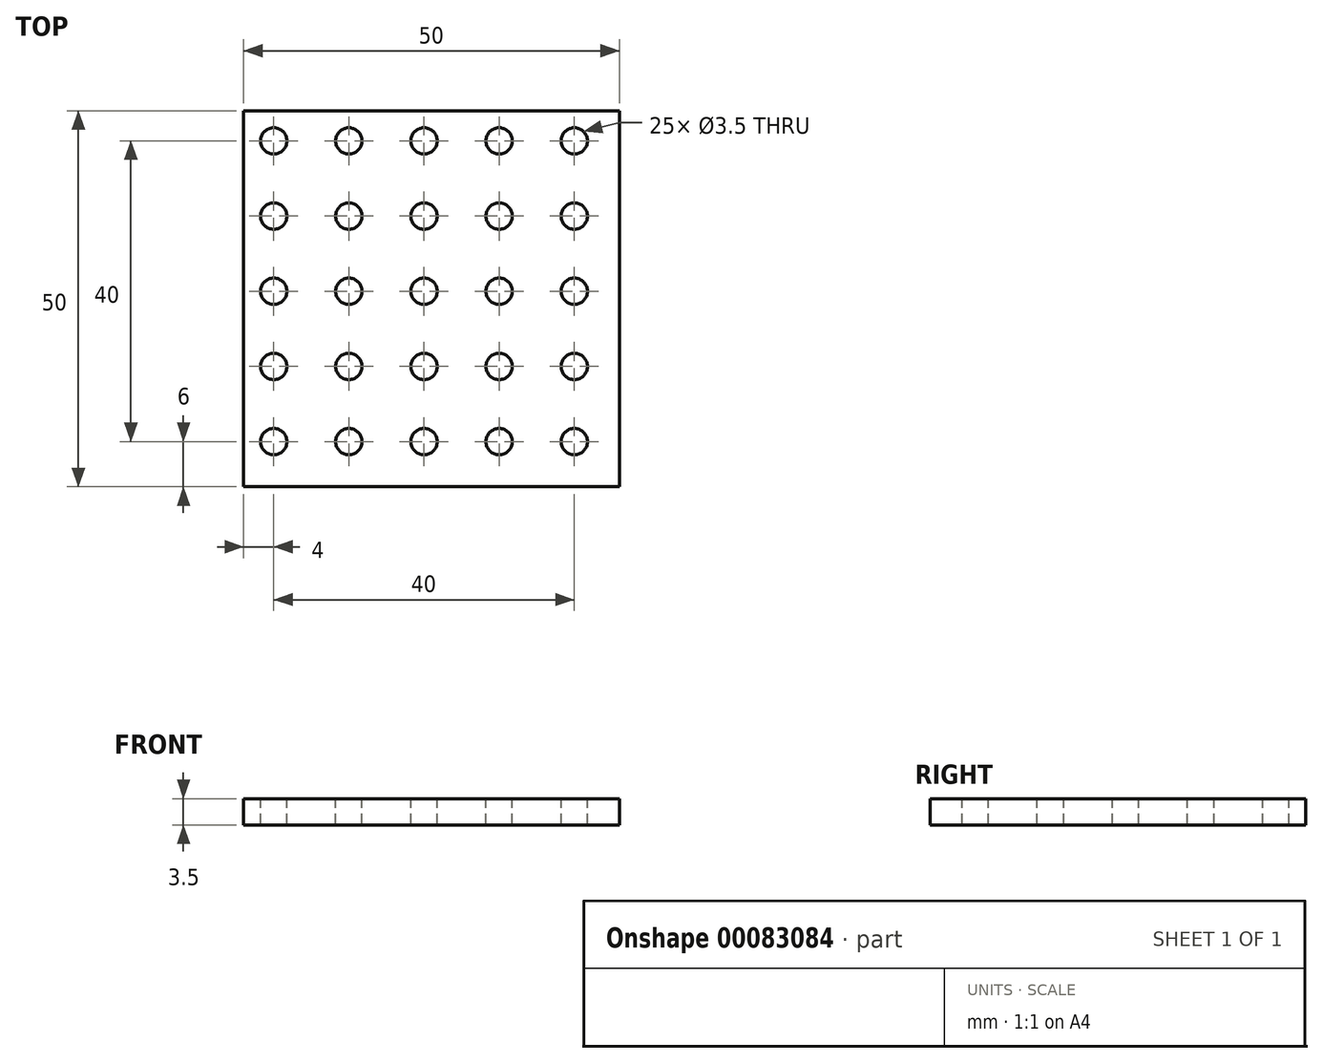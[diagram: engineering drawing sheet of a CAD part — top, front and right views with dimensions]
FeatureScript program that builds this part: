
annotation { "Feature Type Name" : "Feature", "Feature Type Description" : "" }
export const myFeature = defineFeature(function(context is Context, id is Id, definition is map)
    precondition{}
    {
        {
            var Q0;
            Q0=qCreatedBy(makeId("Top.planeOp"),FACE);
            var sketch = newSketch(context, id + "F0", { "sketchPlane" : qUnion([Q0])});
            skLineSegment(sketch, "E0", {"start": v(0, 0) * mm, "end": v(50, 0) * mm});
            skLineSegment(sketch, "E1", {"start": v(50, 0) * mm, "end": v(50, -50) * mm});
            skLineSegment(sketch, "E2", {"start": v(50, -50) * mm, "end": v(0, -50) * mm});
            skLineSegment(sketch, "E3", {"start": v(0, -50) * mm, "end": v(0, 0) * mm});
            skSolve(sketch);
        }
        {
            var Q0;
            Q0=makeQuery(id+"F0.imprint","IMPRINT",FACE,{"disambiguationData":[TD([[makeQuery(id+"F0.imprint","IMPRINT",EDGE,{"derivedFrom":sQuery(id+"F0.wireOp",EDGE,"E0")}),-1.0]])]});
            extrude(context, id + "F1", {"entities" : qUnion([Q0]), "depth" : 3.5 * mm});
        }
        {
            var Q0;
            Q0=makeQuery(id+"F1.opExtrude","CAP_FACE",FACE,{"disambiguationData":[OSD([sQuery(id+"F0.wireOp",EDGE,"E0"),sQuery(id+"F0.wireOp",EDGE,"E1"),sQuery(id+"F0.wireOp",EDGE,"E2"),sQuery(id+"F0.wireOp",EDGE,"E3")])],"isStart":false});
            var sketch = newSketch(context, id + "F2", { "sketchPlane" : qUnion([Q0])});
            skLineSegment(sketch, "E4", {"start": v(0, 0) * mm, "end": v(4, 0) * mm, "construction": true});
            skLineSegment(sketch, "E5", {"start": v(4, 0) * mm, "end": v(4, -4) * mm, "construction": true});
            skCircle(sketch, "E6", {"center": v(4, -4) * mm, "radius": 1.75 * mm});
            skCircle(sketch, "E7.0.1.0", {"center": v(4, -14) * mm, "radius": 1.75 * mm});
            skCircle(sketch, "E7.0.2.0", {"center": v(4, -24) * mm, "radius": 1.75 * mm});
            skCircle(sketch, "E7.0.3.0", {"center": v(4, -34) * mm, "radius": 1.75 * mm});
            skCircle(sketch, "E7.0.4.0", {"center": v(4, -44) * mm, "radius": 1.75 * mm});
            skCircle(sketch, "E7.1.0.0", {"center": v(14, -4) * mm, "radius": 1.75 * mm});
            skCircle(sketch, "E7.1.1.0", {"center": v(14, -14) * mm, "radius": 1.75 * mm});
            skCircle(sketch, "E7.1.2.0", {"center": v(14, -24) * mm, "radius": 1.75 * mm});
            skCircle(sketch, "E7.1.3.0", {"center": v(14, -34) * mm, "radius": 1.75 * mm});
            skCircle(sketch, "E7.1.4.0", {"center": v(14, -44) * mm, "radius": 1.75 * mm});
            skCircle(sketch, "E7.2.0.0", {"center": v(24, -4) * mm, "radius": 1.75 * mm});
            skCircle(sketch, "E7.2.1.0", {"center": v(24, -14) * mm, "radius": 1.75 * mm});
            skCircle(sketch, "E7.2.2.0", {"center": v(24, -24) * mm, "radius": 1.75 * mm});
            skCircle(sketch, "E7.2.3.0", {"center": v(24, -34) * mm, "radius": 1.75 * mm});
            skCircle(sketch, "E7.2.4.0", {"center": v(24, -44) * mm, "radius": 1.75 * mm});
            skCircle(sketch, "E7.3.0.0", {"center": v(34, -4) * mm, "radius": 1.75 * mm});
            skCircle(sketch, "E7.3.1.0", {"center": v(34, -14) * mm, "radius": 1.75 * mm});
            skCircle(sketch, "E7.3.2.0", {"center": v(34, -24) * mm, "radius": 1.75 * mm});
            skCircle(sketch, "E7.3.3.0", {"center": v(34, -34) * mm, "radius": 1.75 * mm});
            skCircle(sketch, "E7.3.4.0", {"center": v(34, -44) * mm, "radius": 1.75 * mm});
            skCircle(sketch, "E7.4.0.0", {"center": v(44, -4) * mm, "radius": 1.75 * mm});
            skCircle(sketch, "E7.4.1.0", {"center": v(44, -14) * mm, "radius": 1.75 * mm});
            skCircle(sketch, "E7.4.2.0", {"center": v(44, -24) * mm, "radius": 1.75 * mm});
            skCircle(sketch, "E7.4.3.0", {"center": v(44, -34) * mm, "radius": 1.75 * mm});
            skCircle(sketch, "E7.4.4.0", {"center": v(44, -44) * mm, "radius": 1.75 * mm});
            skLineSegment(sketch, "E7.direction1", {"start": v(4, -4) * mm, "end": v(14, -4) * mm, "construction": true});
            skLineSegment(sketch, "E7.direction2", {"start": v(4, -4) * mm, "end": v(4, -14) * mm, "construction": true});
            skSolve(sketch);
        }
        {
            var Q0;
            Q0=makeQuery(id+"F2.imprint","IMPRINT",FACE,{"disambiguationData":[TD([[makeQuery(id+"F2.imprint","IMPRINT",EDGE,{"derivedFrom":sQuery(id+"F2.wireOp",EDGE,"E6")}),1.0]])]});
            var Q1;
            Q1=makeQuery(id+"F2.imprint","IMPRINT",FACE,{"disambiguationData":[TD([[makeQuery(id+"F2.imprint","IMPRINT",EDGE,{"derivedFrom":sQuery(id+"F2.wireOp",EDGE,"E7.1.0.0")}),1.0]])]});
            var Q2;
            Q2=makeQuery(id+"F2.imprint","IMPRINT",FACE,{"disambiguationData":[TD([[makeQuery(id+"F2.imprint","IMPRINT",EDGE,{"derivedFrom":sQuery(id+"F2.wireOp",EDGE,"E7.2.0.0")}),1.0]])]});
            var Q3;
            Q3=makeQuery(id+"F2.imprint","IMPRINT",FACE,{"disambiguationData":[TD([[makeQuery(id+"F2.imprint","IMPRINT",EDGE,{"derivedFrom":sQuery(id+"F2.wireOp",EDGE,"E7.3.0.0")}),1.0]])]});
            var Q4;
            Q4=makeQuery(id+"F2.imprint","IMPRINT",FACE,{"disambiguationData":[TD([[makeQuery(id+"F2.imprint","IMPRINT",EDGE,{"derivedFrom":sQuery(id+"F2.wireOp",EDGE,"E7.4.0.0")}),1.0]])]});
            var Q5;
            Q5=makeQuery(id+"F2.imprint","IMPRINT",FACE,{"disambiguationData":[TD([[makeQuery(id+"F2.imprint","IMPRINT",EDGE,{"derivedFrom":sQuery(id+"F2.wireOp",EDGE,"E7.4.1.0")}),1.0]])]});
            var Q6;
            Q6=makeQuery(id+"F2.imprint","IMPRINT",FACE,{"disambiguationData":[TD([[makeQuery(id+"F2.imprint","IMPRINT",EDGE,{"derivedFrom":sQuery(id+"F2.wireOp",EDGE,"E7.3.1.0")}),1.0]])]});
            var Q7;
            Q7=makeQuery(id+"F2.imprint","IMPRINT",FACE,{"disambiguationData":[TD([[makeQuery(id+"F2.imprint","IMPRINT",EDGE,{"derivedFrom":sQuery(id+"F2.wireOp",EDGE,"E7.2.1.0")}),1.0]])]});
            var Q8;
            Q8=makeQuery(id+"F2.imprint","IMPRINT",FACE,{"disambiguationData":[TD([[makeQuery(id+"F2.imprint","IMPRINT",EDGE,{"derivedFrom":sQuery(id+"F2.wireOp",EDGE,"E7.1.1.0")}),1.0]])]});
            var Q9;
            Q9=makeQuery(id+"F2.imprint","IMPRINT",FACE,{"disambiguationData":[TD([[makeQuery(id+"F2.imprint","IMPRINT",EDGE,{"derivedFrom":sQuery(id+"F2.wireOp",EDGE,"E7.0.1.0")}),1.0]])]});
            var Q10;
            Q10=makeQuery(id+"F2.imprint","IMPRINT",FACE,{"disambiguationData":[TD([[makeQuery(id+"F2.imprint","IMPRINT",EDGE,{"derivedFrom":sQuery(id+"F2.wireOp",EDGE,"E7.0.2.0")}),1.0]])]});
            var Q11;
            Q11=makeQuery(id+"F2.imprint","IMPRINT",FACE,{"disambiguationData":[TD([[makeQuery(id+"F2.imprint","IMPRINT",EDGE,{"derivedFrom":sQuery(id+"F2.wireOp",EDGE,"E7.1.2.0")}),1.0]])]});
            var Q12;
            Q12=makeQuery(id+"F2.imprint","IMPRINT",FACE,{"disambiguationData":[TD([[makeQuery(id+"F2.imprint","IMPRINT",EDGE,{"derivedFrom":sQuery(id+"F2.wireOp",EDGE,"E7.2.2.0")}),1.0]])]});
            var Q13;
            Q13=makeQuery(id+"F2.imprint","IMPRINT",FACE,{"disambiguationData":[TD([[makeQuery(id+"F2.imprint","IMPRINT",EDGE,{"derivedFrom":sQuery(id+"F2.wireOp",EDGE,"E7.3.2.0")}),1.0]])]});
            var Q14;
            Q14=makeQuery(id+"F2.imprint","IMPRINT",FACE,{"disambiguationData":[TD([[makeQuery(id+"F2.imprint","IMPRINT",EDGE,{"derivedFrom":sQuery(id+"F2.wireOp",EDGE,"E7.4.2.0")}),1.0]])]});
            var Q15;
            Q15=makeQuery(id+"F2.imprint","IMPRINT",FACE,{"disambiguationData":[TD([[makeQuery(id+"F2.imprint","IMPRINT",EDGE,{"derivedFrom":sQuery(id+"F2.wireOp",EDGE,"E7.0.3.0")}),1.0]])]});
            var Q16;
            Q16=makeQuery(id+"F2.imprint","IMPRINT",FACE,{"disambiguationData":[TD([[makeQuery(id+"F2.imprint","IMPRINT",EDGE,{"derivedFrom":sQuery(id+"F2.wireOp",EDGE,"E7.1.3.0")}),1.0]])]});
            var Q17;
            Q17=makeQuery(id+"F2.imprint","IMPRINT",FACE,{"disambiguationData":[TD([[makeQuery(id+"F2.imprint","IMPRINT",EDGE,{"derivedFrom":sQuery(id+"F2.wireOp",EDGE,"E7.2.3.0")}),1.0]])]});
            var Q18;
            Q18=makeQuery(id+"F2.imprint","IMPRINT",FACE,{"disambiguationData":[TD([[makeQuery(id+"F2.imprint","IMPRINT",EDGE,{"derivedFrom":sQuery(id+"F2.wireOp",EDGE,"E7.3.3.0")}),1.0]])]});
            var Q19;
            Q19=makeQuery(id+"F2.imprint","IMPRINT",FACE,{"disambiguationData":[TD([[makeQuery(id+"F2.imprint","IMPRINT",EDGE,{"derivedFrom":sQuery(id+"F2.wireOp",EDGE,"E7.4.3.0")}),1.0]])]});
            var Q20;
            Q20=makeQuery(id+"F2.imprint","IMPRINT",FACE,{"disambiguationData":[TD([[makeQuery(id+"F2.imprint","IMPRINT",EDGE,{"derivedFrom":sQuery(id+"F2.wireOp",EDGE,"E7.0.4.0")}),1.0]])]});
            var Q21;
            Q21=makeQuery(id+"F2.imprint","IMPRINT",FACE,{"disambiguationData":[TD([[makeQuery(id+"F2.imprint","IMPRINT",EDGE,{"derivedFrom":sQuery(id+"F2.wireOp",EDGE,"E7.1.4.0")}),1.0]])]});
            var Q22;
            Q22=makeQuery(id+"F2.imprint","IMPRINT",FACE,{"disambiguationData":[TD([[makeQuery(id+"F2.imprint","IMPRINT",EDGE,{"derivedFrom":sQuery(id+"F2.wireOp",EDGE,"E7.2.4.0")}),1.0]])]});
            var Q23;
            Q23=makeQuery(id+"F2.imprint","IMPRINT",FACE,{"disambiguationData":[TD([[makeQuery(id+"F2.imprint","IMPRINT",EDGE,{"derivedFrom":sQuery(id+"F2.wireOp",EDGE,"E7.3.4.0")}),1.0]])]});
            var Q24;
            Q24=makeQuery(id+"F2.imprint","IMPRINT",FACE,{"disambiguationData":[TD([[makeQuery(id+"F2.imprint","IMPRINT",EDGE,{"derivedFrom":sQuery(id+"F2.wireOp",EDGE,"E7.4.4.0")}),1.0]])]});
            extrude(context, id + "F3", {"entities" : qUnion([Q0, Q1, Q2, Q3, Q4, Q5, Q6, Q7, Q8, Q9, Q10, Q11, Q12, Q13, Q14, Q15, Q16, Q17, Q18, Q19, Q20, Q21, Q22, Q23, Q24]), "operationType" : NewBodyOperationType.REMOVE, "endBound" : BoundingType.THROUGH_ALL, "oppositeDirection" : true, "depth" : 25 * mm});
        }
    });
